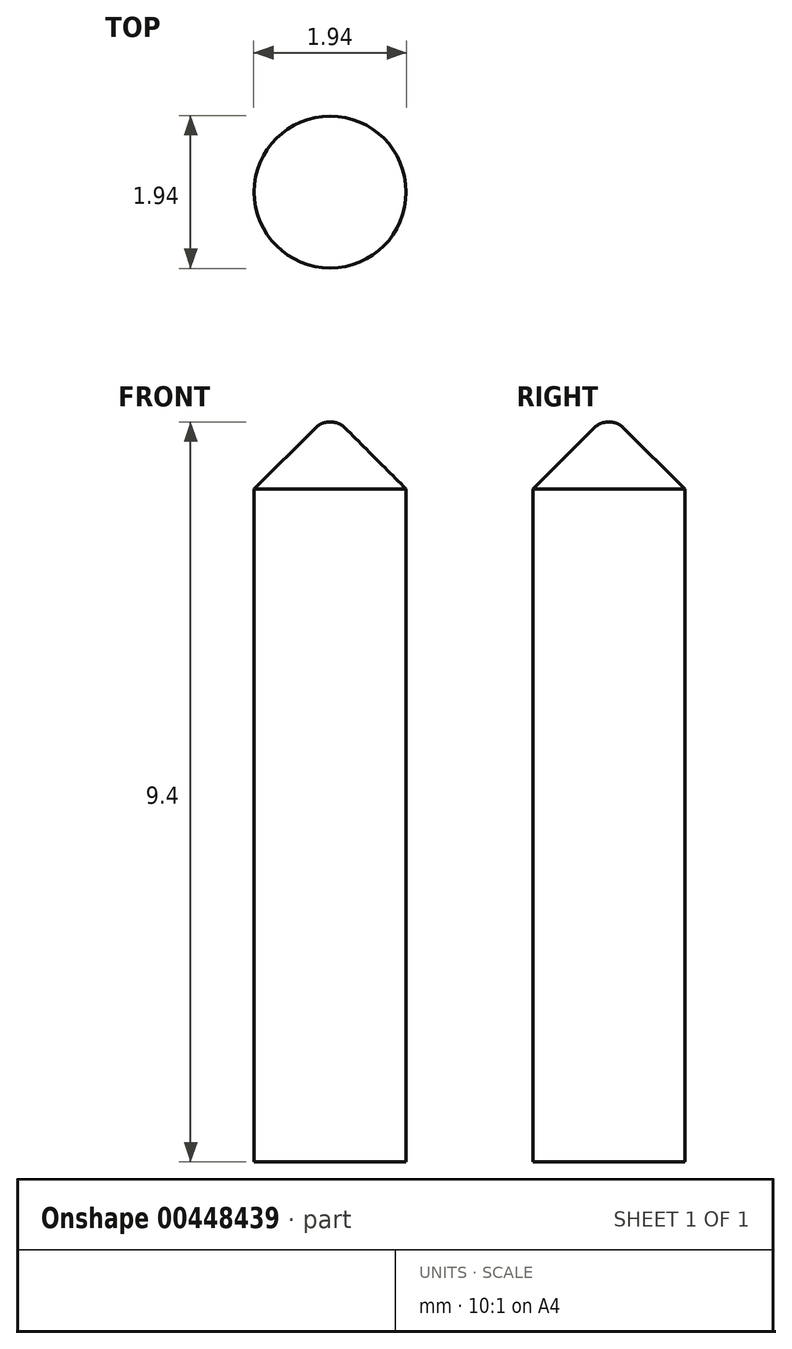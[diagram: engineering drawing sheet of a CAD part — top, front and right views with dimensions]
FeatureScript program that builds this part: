
annotation { "Feature Type Name" : "Feature", "Feature Type Description" : "" }
export const myFeature = defineFeature(function(context is Context, id is Id, definition is map)
    precondition{}
    {
        {
            var Q0;
            Q0=qCreatedBy(makeId("Top.planeOp"),FACE);
            var sketch = newSketch(context, id + "F0", { "sketchPlane" : qUnion([Q0])});
            skCircle(sketch, "E0", {"center": v(0, 0) * mm, "radius": 0.97 * mm});
            skSolve(sketch);
        }
        {
            var Q0;
            Q0=makeQuery(id+"F0.imprint","IMPRINT",FACE,{"disambiguationData":[TD([[makeQuery(id+"F0.imprint","IMPRINT",EDGE,{"derivedFrom":sQuery(id+"F0.wireOp",EDGE,"E0")}),1.0]])]});
            extrude(context, id + "F1", {"entities" : qUnion([Q0]), "depth" : 9.4 * mm});
        }
        {
            var Q0;
            Q0=makeQuery(id+"F1.opExtrude","CAP_EDGE",EDGE,{"disambiguationData":[OSD([sQuery(id+"F0.wireOp",EDGE,"E0")])],"isStart":false});
            chamfer(context, id + "F2", {"entities" : qUnion([Q0]), "width" : 0.85 * mm, "tangentPropagation" : true});
        }
        {
            var Q0;
            {var subQ0=sQuery(id+"F0.wireOp",EDGE,"E0");Q0=makeQuery(id+"F2.opChamfer","BLEND_EDGE",EDGE,{"blendedFrom":[makeQuery(id+"F1.opExtrude","CAP_EDGE",EDGE,{"disambiguationData":[OSD([subQ0])],"isStart":false}),makeQuery(id+"F1.opExtrude","CAP_FACE",FACE,{"disambiguationData":[OSD([subQ0])],"isStart":false})],"blendedInto":[makeQuery(id+"F1.opExtrude","CAP_FACE",FACE,{"disambiguationData":[OSD([subQ0])],"isStart":false})]});}
            fillet(context, id + "F3", {"entities" : qUnion([Q0]), "radius" : 0.25 * mm, "tangentPropagation" : true, "allowEdgeOverflow" : false});
        }
    });
